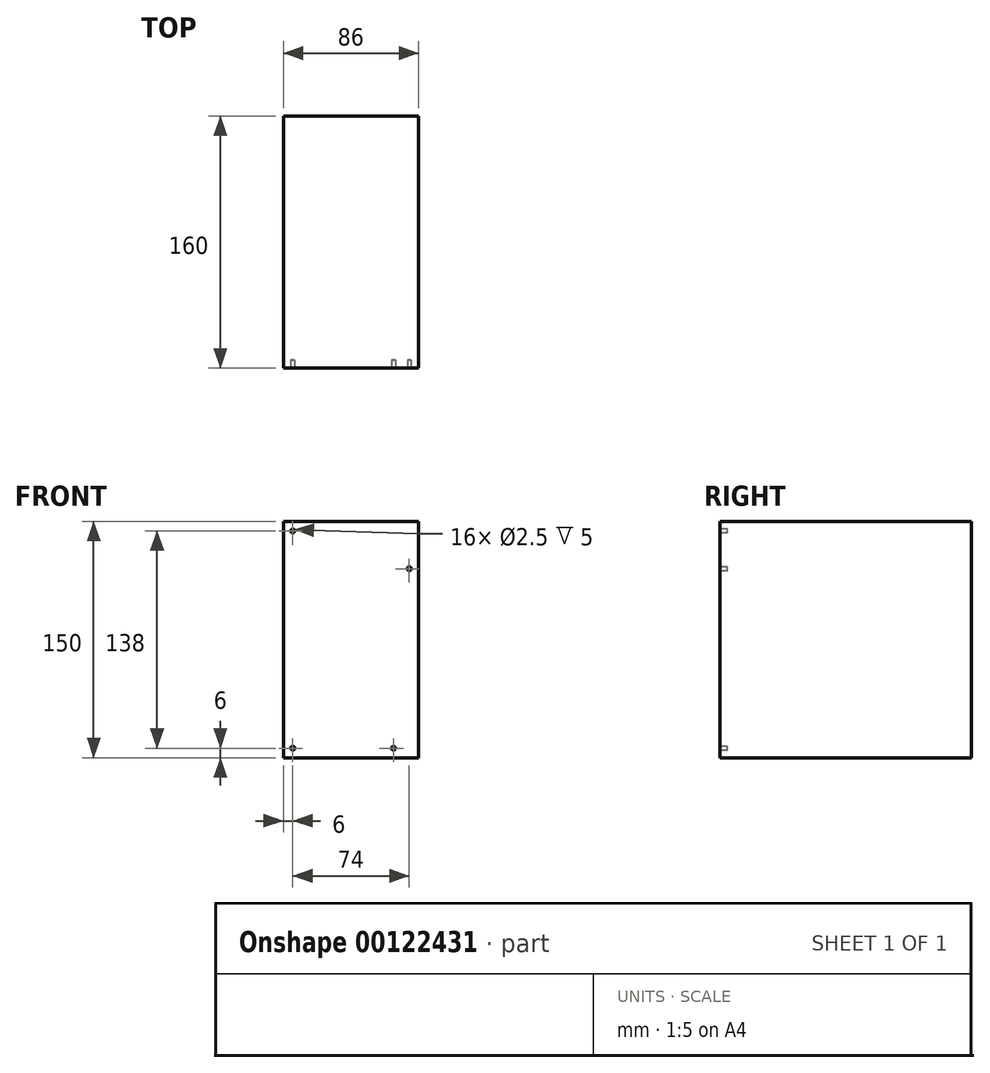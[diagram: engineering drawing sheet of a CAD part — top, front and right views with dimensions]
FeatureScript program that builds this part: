
annotation { "Feature Type Name" : "Feature", "Feature Type Description" : "" }
export const myFeature = defineFeature(function(context is Context, id is Id, definition is map)
    precondition{}
    {
        {
            var Q0;
            Q0=qCreatedBy(makeId("Front.planeOp"),FACE);
            var sketch = newSketch(context, id + "F0", { "sketchPlane" : qUnion([Q0])});
            skLineSegment(sketch, "E0.bottom", {"start": v(0, 0) * mm, "end": v(86, 0) * mm});
            skLineSegment(sketch, "E0.top", {"start": v(0, 150) * mm, "end": v(86, 150) * mm});
            skLineSegment(sketch, "E0.left", {"start": v(0, 0) * mm, "end": v(0, 150) * mm});
            skLineSegment(sketch, "E0.right", {"start": v(86, 0) * mm, "end": v(86, 150) * mm});
            skSolve(sketch);
        }
        {
            var Q0;
            Q0 = qSketchRegion(id + "F0", true);
            extrude(context, id + "F1", {"entities" : qUnion([Q0]), "oppositeDirection" : true, "depth" : 160 * mm});
        }
        {
            var Q0;
            Q0=makeQuery(id+"F1.opExtrude","CAP_FACE",FACE,{"disambiguationData":[OSD([sQuery(id+"F0.wireOp",EDGE,"E0.bottom"),sQuery(id+"F0.wireOp",EDGE,"E0.top"),sQuery(id+"F0.wireOp",EDGE,"E0.left"),sQuery(id+"F0.wireOp",EDGE,"E0.right")])],"isStart":true});
            var sketch = newSketch(context, id + "F2", { "sketchPlane" : qUnion([Q0])});
            skCircle(sketch, "E1", {"center": v(6, 6) * mm, "radius": 1.25 * mm});
            skCircle(sketch, "E2", {"center": v(70, 6) * mm, "radius": 1.25 * mm});
            skCircle(sketch, "E3", {"center": v(80, 120) * mm, "radius": 1.25 * mm});
            skCircle(sketch, "E4", {"center": v(6, 144) * mm, "radius": 1.25 * mm});
            skSolve(sketch);
        }
        {
            var Q0;
            Q0 = qSketchRegion(id + "F2", true);
            extrude(context, id + "F3", {"entities" : qUnion([Q0]), "operationType" : NewBodyOperationType.REMOVE, "oppositeDirection" : true, "depth" : 5 * mm});
        }
    });
